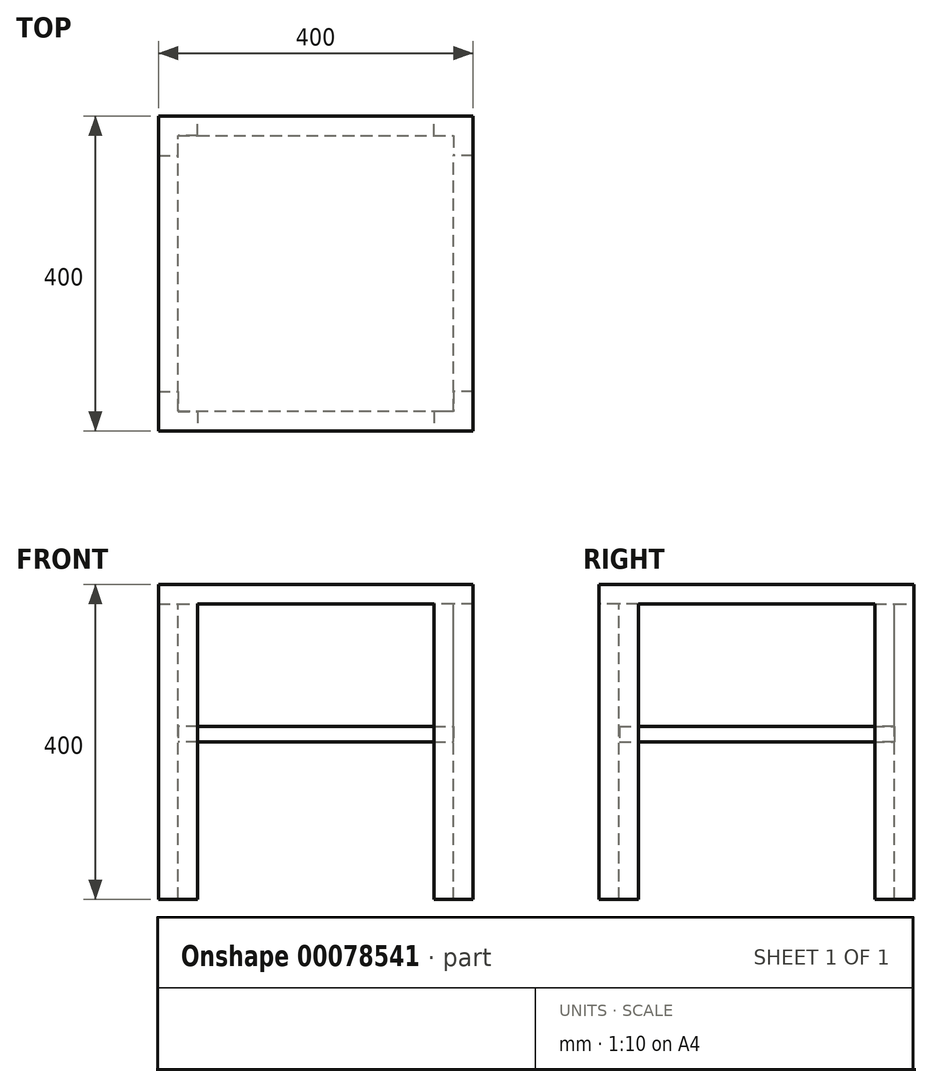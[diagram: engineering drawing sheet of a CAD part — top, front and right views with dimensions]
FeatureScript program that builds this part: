
annotation { "Feature Type Name" : "Feature", "Feature Type Description" : "" }
export const myFeature = defineFeature(function(context is Context, id is Id, definition is map)
    precondition{}
    {
        {
            var Q0;
            Q0=qCreatedBy(makeId("Top.planeOp"),FACE);
            cPlane(context, id + "F0", {"entities" : qUnion([Q0]), "cplaneType" : CPlaneType.OFFSET, "offset" : 400 * mm, "width" : 150 * mm, "height" : 150 * mm});
        }
        {
            var Q0;
            Q0=qCreatedBy(id+"F0.planeOp",FACE);
            var sketch = newSketch(context, id + "F1", { "sketchPlane" : qUnion([Q0])});
            skLineSegment(sketch, "E0.bottom", {"start": v(-200, 200) * mm, "end": v(200, 200) * mm});
            skLineSegment(sketch, "E0.top", {"start": v(-200, -200) * mm, "end": v(200, -200) * mm});
            skLineSegment(sketch, "E0.left", {"start": v(-200, 200) * mm, "end": v(-200, -200) * mm});
            skLineSegment(sketch, "E0.right", {"start": v(200, 200) * mm, "end": v(200, -200) * mm});
            skSolve(sketch);
        }
        {
            var Q0;
            Q0 = qSketchRegion(id + "F1", true);
            extrude(context, id + "F2", {"entities" : qUnion([Q0]), "oppositeDirection" : true, "depth" : 25 * mm});
        }
        {
            var Q0;
            Q0=makeQuery(id+"F2.opExtrude","CAP_FACE",FACE,{"disambiguationData":[OSD([sQuery(id+"F1.wireOp",EDGE,"E0.bottom"),sQuery(id+"F1.wireOp",EDGE,"E0.top"),sQuery(id+"F1.wireOp",EDGE,"E0.left"),sQuery(id+"F1.wireOp",EDGE,"E0.right")])],"isStart":false});
            var sketch = newSketch(context, id + "F3", { "sketchPlane" : qUnion([Q0])});
            skLineSegment(sketch, "E1", {"start": v(-200, 150) * mm, "end": v(-175, 150) * mm});
            skLineSegment(sketch, "E2", {"start": v(-175, 150) * mm, "end": v(-175, 175) * mm});
            skLineSegment(sketch, "E3", {"start": v(-175, 175) * mm, "end": v(-150, 175) * mm});
            skLineSegment(sketch, "E4", {"start": v(-150, 175) * mm, "end": v(-150, 200) * mm});
            skLineSegment(sketch, "E5", {"start": v(-150, 200) * mm, "end": v(-200, 200) * mm});
            skLineSegment(sketch, "E6", {"start": v(-200, 200) * mm, "end": v(-200, 150) * mm});
            skLineSegment(sketch, "E7.MirrorCS", {"start": v(200, 150) * mm, "end": v(175, 150) * mm});
            skLineSegment(sketch, "E8.MirrorCS", {"start": v(175, 150) * mm, "end": v(175, 175) * mm});
            skLineSegment(sketch, "E9.MirrorCS", {"start": v(175, 175) * mm, "end": v(150, 175) * mm});
            skLineSegment(sketch, "E10.MirrorCS", {"start": v(150, 175) * mm, "end": v(150, 200) * mm});
            skLineSegment(sketch, "E11.MirrorCS", {"start": v(200, 200) * mm, "end": v(200, 150) * mm});
            skLineSegment(sketch, "E12.MirrorCS", {"start": v(150, 200) * mm, "end": v(200, 200) * mm});
            skLineSegment(sketch, "E13.MirrorCS", {"start": v(-175, -175) * mm, "end": v(-150, -175) * mm});
            skLineSegment(sketch, "E14.MirrorCS", {"start": v(200, -150) * mm, "end": v(175, -150) * mm});
            skLineSegment(sketch, "E15.MirrorCS", {"start": v(-200, -150) * mm, "end": v(-175, -150) * mm});
            skLineSegment(sketch, "E16.MirrorCS", {"start": v(-175, -150) * mm, "end": v(-175, -175) * mm});
            skLineSegment(sketch, "E17.MirrorCS", {"start": v(-150, -175) * mm, "end": v(-150, -200) * mm});
            skLineSegment(sketch, "E18.MirrorCS", {"start": v(-150, -200) * mm, "end": v(-200, -200) * mm});
            skLineSegment(sketch, "E19.MirrorCS", {"start": v(-200, -200) * mm, "end": v(-200, -150) * mm});
            skLineSegment(sketch, "E20.MirrorCS", {"start": v(175, -150) * mm, "end": v(175, -175) * mm});
            skLineSegment(sketch, "E21.MirrorCS", {"start": v(175, -175) * mm, "end": v(150, -175) * mm});
            skLineSegment(sketch, "E22.MirrorCS", {"start": v(150, -200) * mm, "end": v(200, -200) * mm});
            skLineSegment(sketch, "E23.MirrorCS", {"start": v(150, -175) * mm, "end": v(150, -200) * mm});
            skLineSegment(sketch, "E24.MirrorCS", {"start": v(200, -200) * mm, "end": v(200, -150) * mm});
            skSolve(sketch);
        }
        {
            var Q0;
            Q0 = qSketchRegion(id + "F3", true);
            extrude(context, id + "F4", {"entities" : qUnion([Q0]), "operationType" : NewBodyOperationType.ADD, "depth" : 375 * mm});
        }
        {
            var Q0;
            Q0=qCreatedBy(makeId("Top.planeOp"),FACE);
            cPlane(context, id + "F5", {"entities" : qUnion([Q0]), "cplaneType" : CPlaneType.OFFSET, "offset" : 200 * mm, "width" : 150 * mm, "height" : 150 * mm});
        }
        {
            var Q0;
            Q0=qCreatedBy(id+"F5.planeOp",FACE);
            var sketch = newSketch(context, id + "F6", { "sketchPlane" : qUnion([Q0])});
            skLineSegment(sketch, "E25.bottom", {"start": v(-174.74, -174.42) * mm, "end": v(175.26, -174.42) * mm});
            skLineSegment(sketch, "E25.top", {"start": v(-174.74, 175.58) * mm, "end": v(175.26, 175.58) * mm});
            skLineSegment(sketch, "E25.left", {"start": v(-174.74, -174.42) * mm, "end": v(-174.74, 175.58) * mm});
            skLineSegment(sketch, "E25.right", {"start": v(175.26, -174.42) * mm, "end": v(175.26, 175.58) * mm});
            skSolve(sketch);
        }
        {
            var Q0;
            Q0 = qSketchRegion(id + "F6", true);
            extrude(context, id + "F7", {"entities" : qUnion([Q0]), "operationType" : NewBodyOperationType.ADD, "depth" : 20 * mm});
        }
    });
